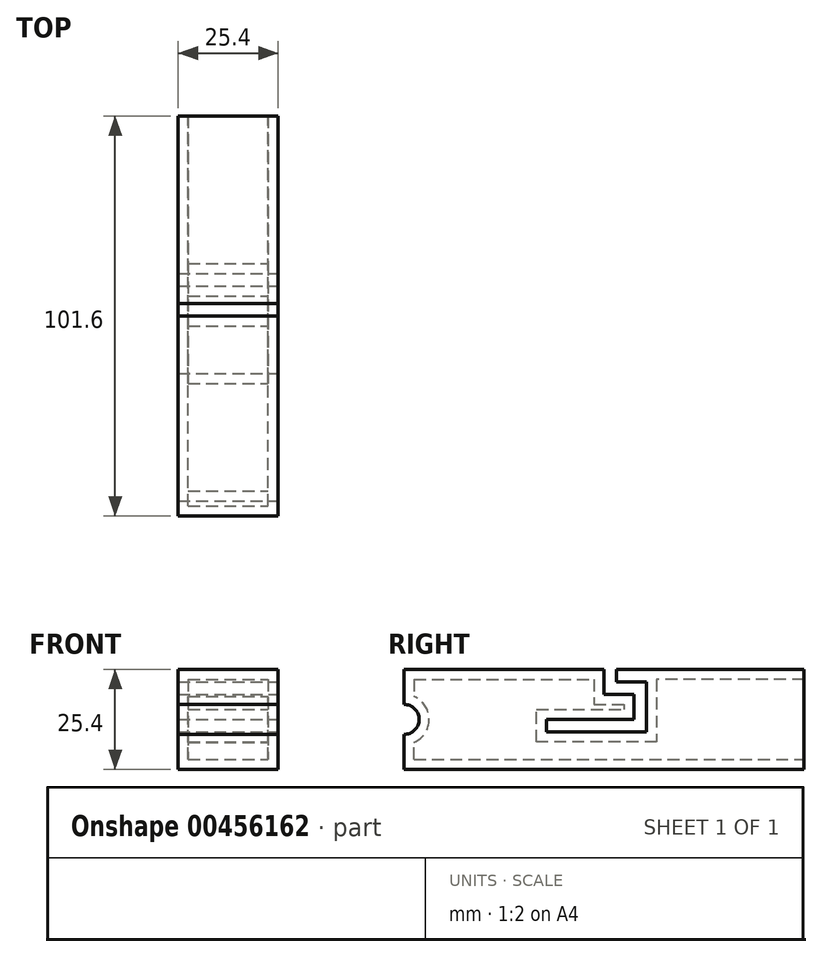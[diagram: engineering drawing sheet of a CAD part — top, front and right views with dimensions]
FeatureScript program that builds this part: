
annotation { "Feature Type Name" : "Feature", "Feature Type Description" : "" }
export const myFeature = defineFeature(function(context is Context, id is Id, definition is map)
    precondition{}
    {
        {
            var Q0;
            Q0=qCreatedBy(makeId("Right.planeOp"),FACE);
            var sketch = newSketch(context, id + "F0", { "sketchPlane" : qUnion([Q0])});
            skLineSegment(sketch, "E0.top", {"start": v(-50.8, -12.7) * mm, "end": v(50.8, -12.7) * mm});
            skLineSegment(sketch, "E0.right", {"start": v(50.8, 12.7) * mm, "end": v(50.8, -12.7) * mm});
            skPoint(sketch, "E0.middle", {"position": v(0, 0) * mm});
            skLineSegment(sketch, "E1", {"start": v(-50.8, 12.7) * mm, "end": v(0, 12.7) * mm});
            skLineSegment(sketch, "E2", {"start": v(50.8, 12.7) * mm, "end": v(3.18, 12.7) * mm});
            skLineSegment(sketch, "E3", {"start": v(3.18, 12.7) * mm, "end": v(3.18, 9.52) * mm});
            skLineSegment(sketch, "E4", {"start": v(0, 12.7) * mm, "end": v(0, 6.35) * mm});
            skLineSegment(sketch, "E5", {"start": v(0, 6.35) * mm, "end": v(7.62, 6.35) * mm});
            skLineSegment(sketch, "E6", {"start": v(7.62, 6.35) * mm, "end": v(7.62, 0) * mm});
            skLineSegment(sketch, "E7", {"start": v(7.62, 0) * mm, "end": v(0, 0) * mm});
            skLineSegment(sketch, "E8", {"start": v(3.18, 9.52) * mm, "end": v(10.8, 9.52) * mm});
            skLineSegment(sketch, "E9", {"start": v(10.8, 9.52) * mm, "end": v(10.8, -3.17) * mm});
            skLineSegment(sketch, "E10", {"start": v(-14.6, -3.18) * mm, "end": v(-14.6, 0) * mm});
            skLineSegment(sketch, "E11", {"start": v(-14.6, 0) * mm, "end": v(0, 0) * mm});
            skLineSegment(sketch, "E12", {"start": v(10.8, -3.17) * mm, "end": v(-14.6, -3.18) * mm});
            skLineSegment(sketch, "E13", {"start": v(-50.8, 12.7) * mm, "end": v(-50.8, 3.81) * mm});
            skLineSegment(sketch, "E14", {"start": v(-50.8, -12.7) * mm, "end": v(-50.8, -3.8) * mm});
            skArc(sketch, "E15", {"start": v(-50.8, -3.8) * mm, "mid": v(-46.99, 0) * mm, "end": v(-50.8, 3.81) * mm});
            skSolve(sketch);
        }
        {
            var Q0;
            Q0=makeQuery(id+"F0.imprint","IMPRINT",FACE,{"disambiguationData":[TD([[makeQuery(id+"F0.imprint","IMPRINT",EDGE,{"derivedFrom":sQuery(id+"F0.wireOp",EDGE,"E0.top")}),1.0]])]});
            var Q1;
            Q1=sQuery(id+"F0.wireOp",EDGE,"E15");
            extrude(context, id + "F1", {"entities" : qUnion([Q0]), "surfaceEntities" : qUnion([Q1]), "endBound" : BoundingType.SYMMETRIC, "oppositeDirection" : true, "depth" : 25.4 * mm});
        }
        {
            var Q0;
            Q0=makeQuery(id+"F1.opExtrude","SWEPT_FACE",FACE,{"disambiguationData":[OSD([sQuery(id+"F0.wireOp",EDGE,"E0.right")])]});
            shell(context, id + "F2", {"entities" : qUnion([Q0]), "thickness" : 2.54 * mm});
        }
    });
